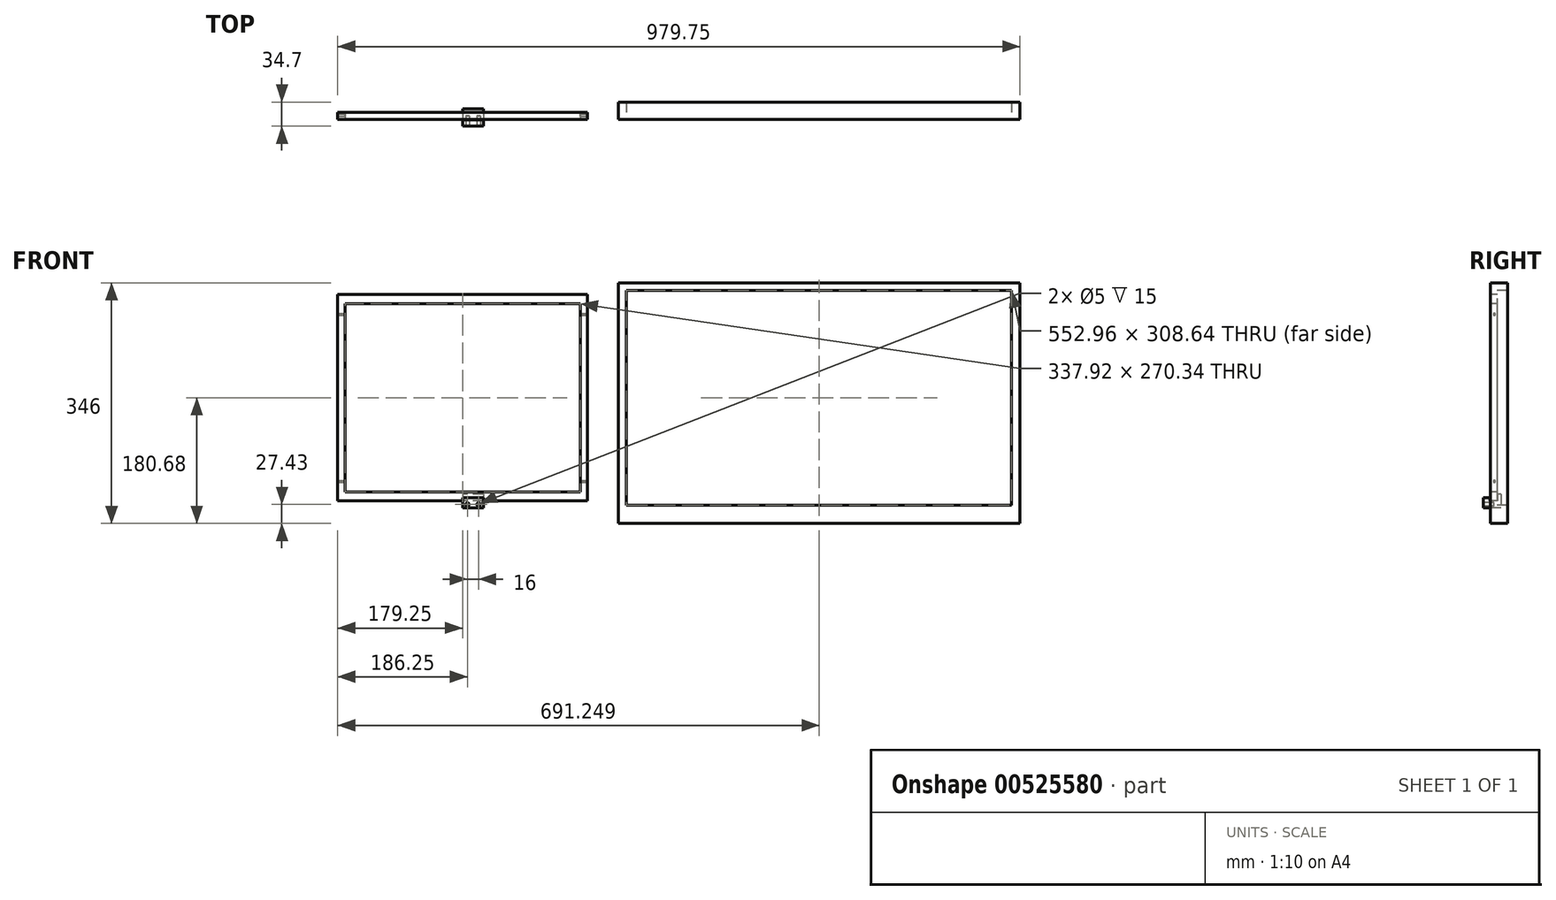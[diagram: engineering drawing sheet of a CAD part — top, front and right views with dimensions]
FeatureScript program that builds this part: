
annotation { "Feature Type Name" : "Feature", "Feature Type Description" : "" }
export const myFeature = defineFeature(function(context is Context, id is Id, definition is map)
    precondition{}
    {
        {
            var Q0;
            Q0=qCreatedBy(makeId("Front.planeOp"),FACE);
            var sketch = newSketch(context, id + "F0", { "sketchPlane" : qUnion([Q0])});
            skLineSegment(sketch, "E0.bottom", {"start": v(168.96, -135.17) * mm, "end": v(-168.96, -135.17) * mm});
            skLineSegment(sketch, "E0.top", {"start": v(168.96, 135.17) * mm, "end": v(-168.96, 135.17) * mm});
            skLineSegment(sketch, "E0.left", {"start": v(168.96, -135.17) * mm, "end": v(168.96, 135.17) * mm});
            skLineSegment(sketch, "E0.right", {"start": v(-168.96, -135.17) * mm, "end": v(-168.96, 135.17) * mm});
            skPoint(sketch, "E0.middle", {"position": v(0, 0) * mm});
            skLineSegment(sketch, "E1.bottom", {"start": v(179.25, -148.25) * mm, "end": v(-179.25, -148.25) * mm});
            skLineSegment(sketch, "E1.top", {"start": v(179.25, 148.25) * mm, "end": v(-179.25, 148.25) * mm});
            skLineSegment(sketch, "E1.left", {"start": v(179.25, -148.25) * mm, "end": v(179.25, 148.25) * mm});
            skLineSegment(sketch, "E1.right", {"start": v(-179.25, -148.25) * mm, "end": v(-179.25, 148.25) * mm});
            skSolve(sketch);
        }
        {
            var Q0;
            Q0=qSketchRegion(id+"F0",true);
            extrude(context, id + "F1", {"entities" : qUnion([Q0]), "oppositeDirection" : true, "depth" : 10.3 * mm});
        }
        {
            var Q0;
            Q0=makeQuery(id+"F1.opExtrude","SWEPT_FACE",FACE,{"disambiguationData":[OSD([sQuery(id+"F0.wireOp",EDGE,"E1.left")])]});
            var sketch = newSketch(context, id + "F2", { "sketchPlane" : qUnion([Q0])});
            skCircle(sketch, "E2", {"center": v(6, 120) * mm, "radius": 1.5 * mm});
            skCircle(sketch, "E3", {"center": v(6, -120) * mm, "radius": 1.5 * mm});
            skSolve(sketch);
        }
        {
            var Q0;
            Q0=qSketchRegion(id+"F2",true);
            extrude(context, id + "F3", {"entities" : qUnion([Q0]), "operationType" : NewBodyOperationType.REMOVE, "oppositeDirection" : true, "depth" : 390 * mm});
        }
        {
            var Q0;
            Q0=qCreatedBy(makeId("Right.planeOp"),FACE);
            var sketch = newSketch(context, id + "F4", { "sketchPlane" : qUnion([Q0])});
            skLineSegment(sketch, "E4.bottom", {"start": v(15.3, -158.25) * mm, "end": v(-9.7, -158.25) * mm});
            skLineSegment(sketch, "E4.left", {"start": v(15.3, -138.25) * mm, "end": v(15.3, -158.25) * mm});
            skLineSegment(sketch, "E4.right", {"start": v(-9.7, -143.25) * mm, "end": v(-9.7, -158.25) * mm});
            skLineSegment(sketch, "E5", {"start": v(15.3, -138.25) * mm, "end": v(10.3, -138.25) * mm});
            skLineSegment(sketch, "E6", {"start": v(10.3, -138.25) * mm, "end": v(10.3, -148.25) * mm});
            skLineSegment(sketch, "E7", {"start": v(10.3, -148.25) * mm, "end": v(-0.7, -148.25) * mm});
            skLineSegment(sketch, "E8", {"start": v(-0.7, -148.25) * mm, "end": v(-0.7, -143.25) * mm});
            skLineSegment(sketch, "E9", {"start": v(-0.7, -143.25) * mm, "end": v(-9.7, -143.25) * mm});
            skSolve(sketch);
        }
        {
            var Q0;
            Q0=qSketchRegion(id+"F4",true);
            extrude(context, id + "F5", {"entities" : qUnion([Q0]), "depth" : 30 * mm});
        }
        {
            var Q0;
            Q0=makeQuery(id+"F5.opExtrude","SWEPT_FACE",FACE,{"disambiguationData":[OSD([sQuery(id+"F4.wireOp",EDGE,"E4.right")])]});
            var sketch = newSketch(context, id + "F6", { "sketchPlane" : qUnion([Q0])});
            skCircle(sketch, "E10", {"center": v(7, -153.25) * mm, "radius": 2.5 * mm});
            skCircle(sketch, "E11", {"center": v(23, -153.25) * mm, "radius": 2.5 * mm});
            skSolve(sketch);
        }
        {
            var Q0;
            Q0=makeQuery(id+"F6.imprint","IMPRINT",FACE,{"disambiguationData":[TD([[makeQuery(id+"F6.imprint","IMPRINT",EDGE,{"derivedFrom":sQuery(id+"F6.wireOp",EDGE,"E10")}),1.0]])]});
            var Q1;
            Q1=makeQuery(id+"F6.imprint","IMPRINT",FACE,{"disambiguationData":[TD([[makeQuery(id+"F6.imprint","IMPRINT",EDGE,{"derivedFrom":sQuery(id+"F6.wireOp",EDGE,"E11")}),1.0]])]});
            extrude(context, id + "F7", {"entities" : qUnion([Q0, Q1]), "operationType" : NewBodyOperationType.REMOVE, "oppositeDirection" : true, "depth" : 15 * mm});
        }
        {
            var Q0;
            Q0=qCreatedBy(makeId("Front.planeOp"),FACE);
            var sketch = newSketch(context, id + "F8", { "sketchPlane" : qUnion([Q0])});
            skLineSegment(sketch, "E12.bottom", {"start": v(788.48, -154.32) * mm, "end": v(235.52, -154.32) * mm});
            skLineSegment(sketch, "E12.top", {"start": v(788.48, 154.32) * mm, "end": v(235.52, 154.32) * mm});
            skLineSegment(sketch, "E12.left", {"start": v(788.48, -154.32) * mm, "end": v(788.48, 154.32) * mm});
            skLineSegment(sketch, "E12.right", {"start": v(235.52, -154.32) * mm, "end": v(235.52, 154.32) * mm});
            skPoint(sketch, "E12.middle", {"position": v(512, 0) * mm});
            skLineSegment(sketch, "E13.bottom", {"start": v(800.5, -180.68) * mm, "end": v(223.5, -180.68) * mm});
            skLineSegment(sketch, "E13.top", {"start": v(800.5, 165.32) * mm, "end": v(223.5, 165.32) * mm});
            skLineSegment(sketch, "E13.left", {"start": v(800.5, -180.68) * mm, "end": v(800.5, 165.32) * mm});
            skLineSegment(sketch, "E13.right", {"start": v(223.5, -180.68) * mm, "end": v(223.5, 165.32) * mm});
            skPoint(sketch, "E13.middle", {"position": v(512, -7.68) * mm});
            skSolve(sketch);
        }
        {
            var Q0;
            Q0=makeQuery(id+"F8.imprint","IMPRINT",FACE,{"disambiguationData":[TD([[makeQuery(id+"F8.imprint","IMPRINT",EDGE,{"derivedFrom":sQuery(id+"F8.wireOp",EDGE,"E12.bottom")}),1.0]])]});
            extrude(context, id + "F9", {"entities" : qUnion([Q0]), "oppositeDirection" : true, "depth" : 25 * mm});
        }
    });
